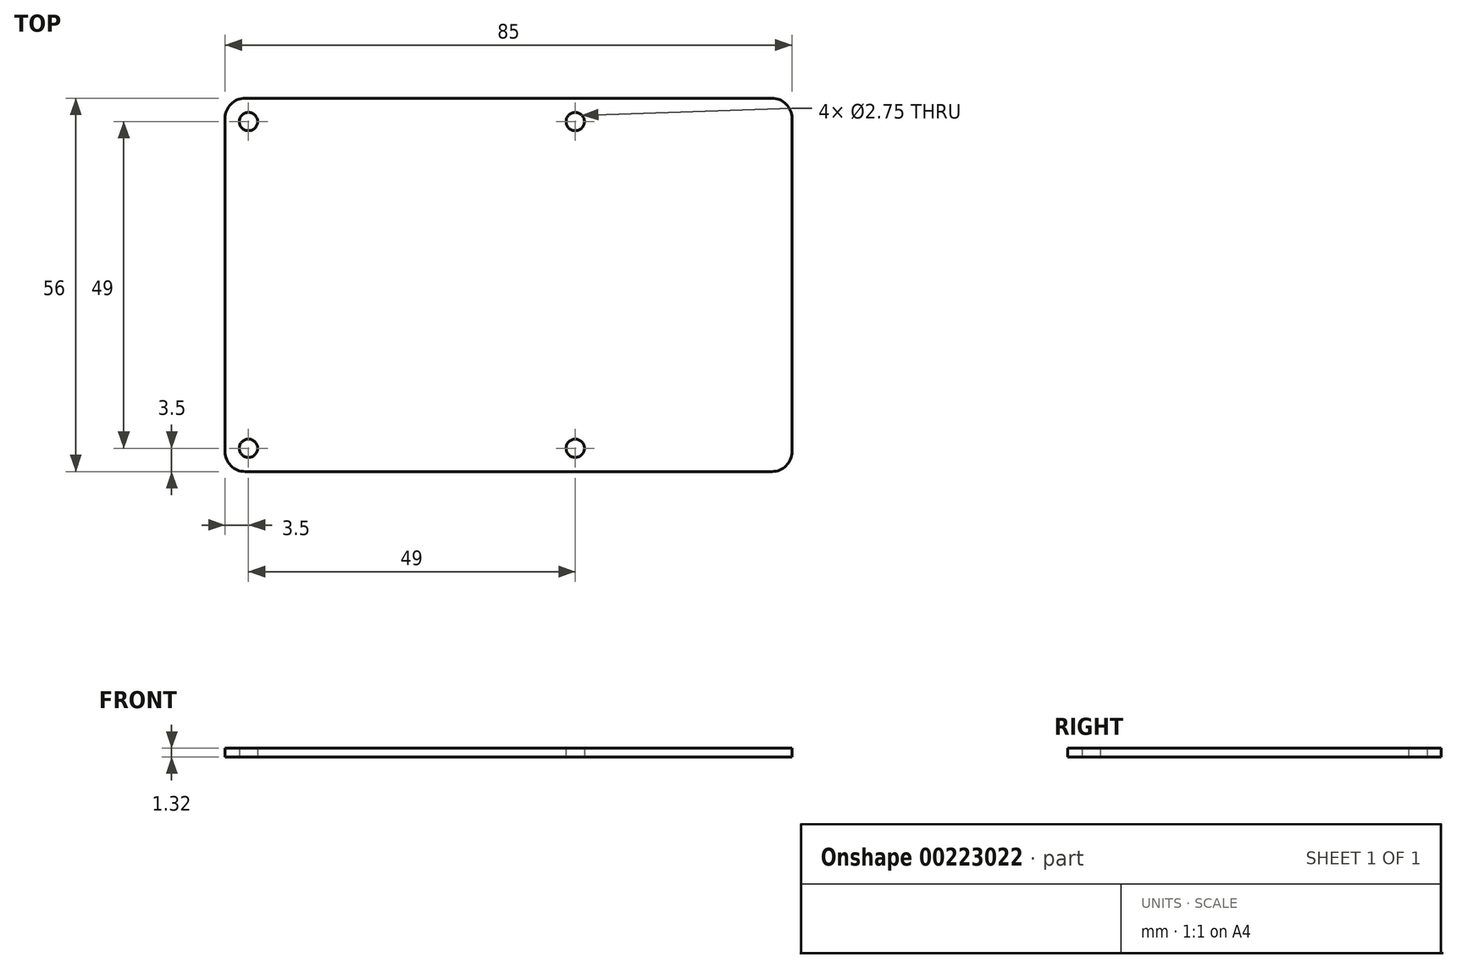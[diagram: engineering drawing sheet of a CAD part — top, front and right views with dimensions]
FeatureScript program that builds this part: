
annotation { "Feature Type Name" : "Feature", "Feature Type Description" : "" }
export const myFeature = defineFeature(function(context is Context, id is Id, definition is map)
    precondition{}
    {
        {
            var Q0;
            Q0=qCreatedBy(makeId("Top.planeOp"),FACE);
            var sketch = newSketch(context, id + "F0", { "sketchPlane" : qUnion([Q0])});
            skLineSegment(sketch, "E0.bottom", {"start": v(39.5, 28) * mm, "end": v(-39.5, 28) * mm});
            skLineSegment(sketch, "E0.top", {"start": v(39.5, -28) * mm, "end": v(-39.5, -28) * mm});
            skLineSegment(sketch, "E0.left", {"start": v(42.5, 25) * mm, "end": v(42.5, -25) * mm});
            skLineSegment(sketch, "E0.right", {"start": v(-42.5, 25) * mm, "end": v(-42.5, -25) * mm});
            skPoint(sketch, "E0.middle", {"position": v(0, 0) * mm});
            skPoint(sketch, "E1", {"position": v(-39, -24.5) * mm});
            skPoint(sketch, "E2.0.1.0", {"position": v(-39, 24.5) * mm});
            skPoint(sketch, "E2.1.0.0", {"position": v(10, -24.5) * mm});
            skPoint(sketch, "E2.1.1.0", {"position": v(10, 24.5) * mm});
            skLineSegment(sketch, "E2.direction1", {"start": v(-39, -24.5) * mm, "end": v(10, -24.5) * mm, "construction": true});
            skLineSegment(sketch, "E2.direction2", {"start": v(-39, -24.5) * mm, "end": v(-39, 24.5) * mm, "construction": true});
            skPoint(sketch, "E3.visualSharp", {"position": v(-42.5, 28) * mm});
            skArc(sketch, "E3.filletArc", {"start": v(-39.5, 28) * mm, "mid": v(-41.62, 27.12) * mm, "end": v(-42.5, 25) * mm});
            skPoint(sketch, "E4.visualSharp", {"position": v(42.5, 28) * mm});
            skArc(sketch, "E4.filletArc", {"start": v(42.5, 25) * mm, "mid": v(41.62, 27.12) * mm, "end": v(39.5, 28) * mm});
            skPoint(sketch, "E5.visualSharp", {"position": v(42.5, -28) * mm});
            skArc(sketch, "E5.filletArc", {"start": v(39.5, -28) * mm, "mid": v(41.62, -27.12) * mm, "end": v(42.5, -25) * mm});
            skPoint(sketch, "E6.visualSharp", {"position": v(-42.5, -28) * mm});
            skArc(sketch, "E6.filletArc", {"start": v(-42.5, -25) * mm, "mid": v(-41.62, -27.12) * mm, "end": v(-39.5, -28) * mm});
            skSolve(sketch);
        }
        {
            var Q0;
            Q0=makeQuery(id+"F0.imprint","IMPRINT",FACE,{"disambiguationData":[TD([[makeQuery(id+"F0.imprint","IMPRINT",EDGE,{"derivedFrom":sQuery(id+"F0.wireOp",EDGE,"E0.bottom")}),1.0]])]});
            extrude(context, id + "F1", {"entities" : qUnion([Q0]), "depth" : 1.32 * mm, "offsetDistance" : 25 * mm});
        }
        {
            var Q0;
            Q0=sQuery(id+"F0.wireOp",VERTEX,"E2.0.1.0");
            var Q1;
            Q1=sQuery(id+"F0.wireOp",VERTEX,"E2.1.1.0");
            var Q2;
            Q2=sQuery(id+"F0.wireOp",VERTEX,"E2.1.0.0");
            var Q3;
            Q3=sQuery(id+"F0.wireOp",VERTEX,"E1");
            var Q4;
            Q4=makeQuery(id+"F1.opExtrude","SWEPT_BODY",BODY,{"disambiguationData":[OSD([sQuery(id+"F0.wireOp",EDGE,"E0.bottom"),sQuery(id+"F0.wireOp",EDGE,"E0.top"),sQuery(id+"F0.wireOp",EDGE,"E0.left"),sQuery(id+"F0.wireOp",EDGE,"E0.right"),sQuery(id+"F0.wireOp",EDGE,"E3.filletArc"),sQuery(id+"F0.wireOp",EDGE,"E4.filletArc"),sQuery(id+"F0.wireOp",EDGE,"E5.filletArc"),sQuery(id+"F0.wireOp",EDGE,"E6.filletArc")])]});
            hole(context, id + "F2", {"style" : HoleStyle.SIMPLE, "endStyle" : HoleEndStyle.THROUGH, "oppositeDirection" : true, "holeDiameter" : 2.75 * mm, "majorDiameter" : 5 * mm, "isTappedThrough" : true, "tappedDepth" : 12 * mm, "tapClearance" : 3, "startFromSketch" : true, "locations" : qUnion([Q0, Q1, Q2, Q3]), "scope" : qUnion([Q4])});
        }
    });
